# Revit family: RV3370 58 Ecodut K2
name_source: partatom
category: Luminarias
revit_build: Autodesk Revit 2015 (Build: 20140606_1530(x64)
units: mm (PartAtom-declared; Revit-internal decimal feet)

## types (6) — shared parameters
Anchura rectángulo de emisión = 228 mm  [stored 0.748031 ft]
Cambio de temperatura de color de luz atenuada = <Ninguno>
Fabricante = SECOM ILUMINACIÓN
Filtro de color = 16777215
Forma visible en renderización = No
Longitud de rectángulo de emisión = 316 mm
Lámpara = LED Osram Oslon SSL
Modelo = Ecodut K2
Ángulo de inclinación = 90.00°

## per-type parameters (varying)
| type | Archivo de red fotométrica | Comentarios de vataje | Descripción |
| Ecodut K2 30W | 3370 58 29 84.IES | 30W | 3370 58 30 84 |
| Ecodut K2 50W | 3370 58 45 84.IES | 50W | 3370 58 50 84 |
| Ecodut K2 70W | 3370 58 61 84.IES | 70W | 3370 58 70 84 |
| Ecodut K2 100W | 3370 58 10 84.IES | 100W | 3370 58 10 84 |
| Ecodut K2 150W |  | 150W | 3370 58 15 84 |
| Ecodut K2 200W | 3370 58 20 84.IES | 200W | 3370 58 20 84 |

note: [stored X ft] marks values corroborated as IEEE doubles in the binary element streams (Revit-internal decimal feet)
